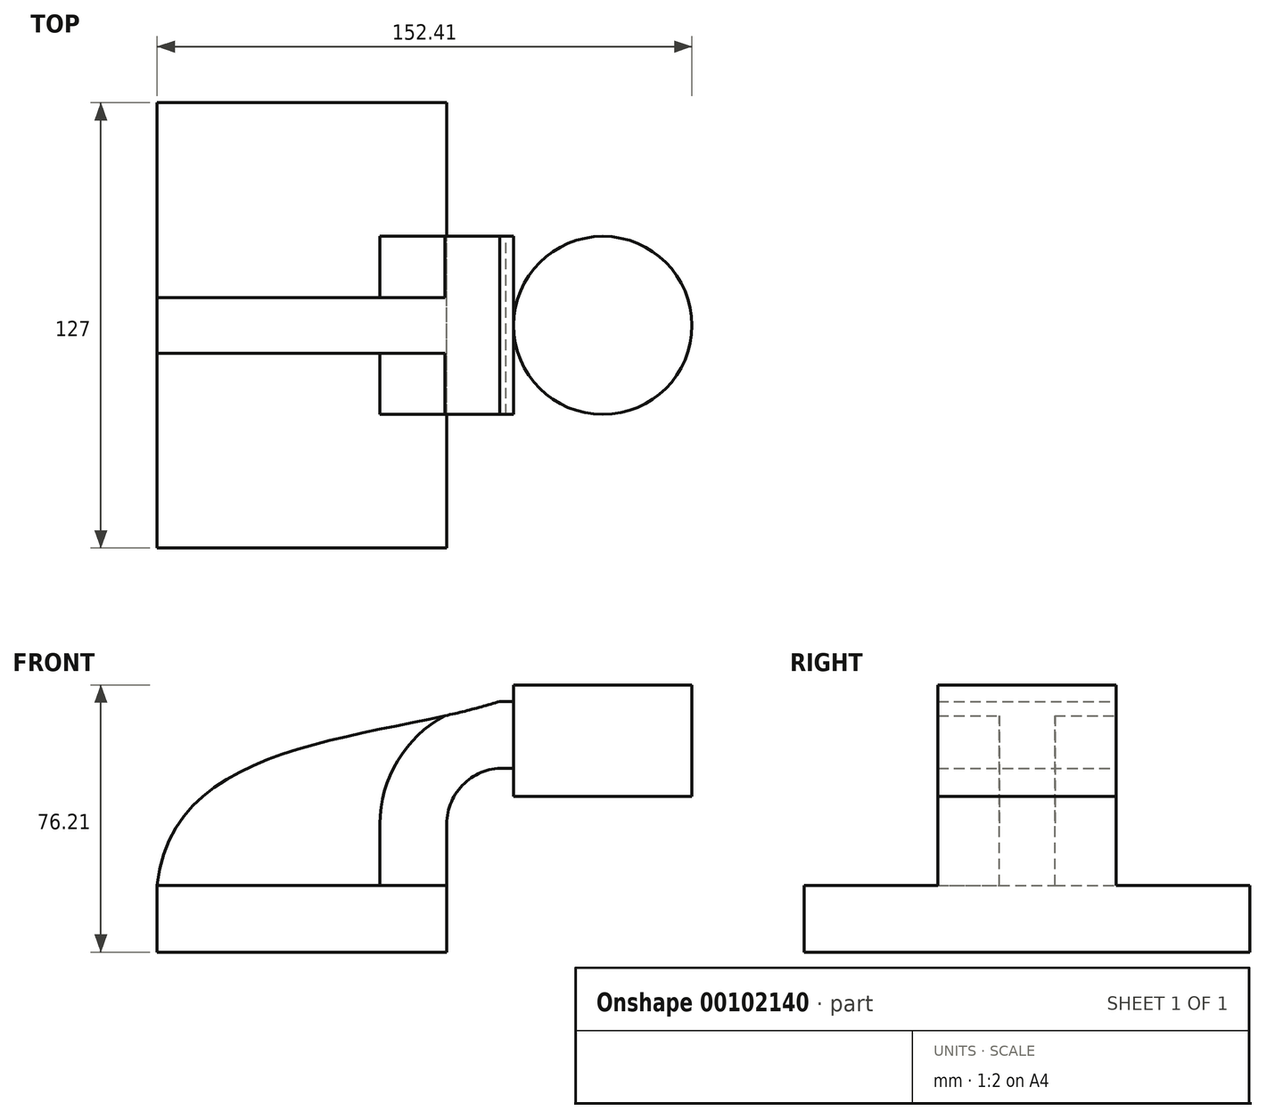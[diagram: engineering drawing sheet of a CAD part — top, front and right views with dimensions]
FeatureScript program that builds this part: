
annotation { "Feature Type Name" : "Feature", "Feature Type Description" : "" }
export const myFeature = defineFeature(function(context is Context, id is Id, definition is map)
    precondition{}
    {
        {
            var Q0;
            Q0=qCreatedBy(makeId("Front.planeOp"),FACE);
            var sketch = newSketch(context, id + "F0", { "sketchPlane" : qUnion([Q0])});
            skLineSegment(sketch, "E0.bottom", {"start": v(-41.28, 9.52) * mm, "end": v(41.28, 9.53) * mm});
            skLineSegment(sketch, "E0.top", {"start": v(-41.28, -9.53) * mm, "end": v(41.28, -9.53) * mm});
            skLineSegment(sketch, "E0.left", {"start": v(-41.28, 9.52) * mm, "end": v(-41.28, -9.53) * mm});
            skLineSegment(sketch, "E0.right", {"start": v(41.28, 9.53) * mm, "end": v(41.28, -9.52) * mm});
            skPoint(sketch, "E0.middle", {"position": v(0, 0) * mm});
            skLineSegment(sketch, "E1.bottom", {"start": v(60.32, 66.68) * mm, "end": v(111.12, 66.68) * mm});
            skLineSegment(sketch, "E1.top", {"start": v(60.32, 34.93) * mm, "end": v(111.12, 34.93) * mm});
            skLineSegment(sketch, "E1.left", {"start": v(60.32, 66.68) * mm, "end": v(60.32, 34.93) * mm});
            skLineSegment(sketch, "E1.right", {"start": v(111.12, 66.68) * mm, "end": v(111.12, 34.93) * mm});
            skPoint(sketch, "E1.middle", {"position": v(85.72, 50.8) * mm});
            skLineSegment(sketch, "E2", {"start": v(41.27, 9.53) * mm, "end": v(41.27, 27.03) * mm});
            skArc(sketch, "E3", {"start": v(41.27, 27.03) * mm, "mid": v(46.3, 38.61) * mm, "end": v(58.17, 42.88) * mm});
            skArc(sketch, "E4.1", {"start": v(22.22, 27.03) * mm, "mid": v(32.17, 51.44) * mm, "end": v(56.33, 61.95) * mm});
            skLineSegment(sketch, "E4.2", {"start": v(22.22, 9.53) * mm, "end": v(22.22, 27.03) * mm});
            skLineSegment(sketch, "E5", {"start": v(56.33, 61.95) * mm, "end": v(85.72, 61.95) * mm});
            skLineSegment(sketch, "E6", {"start": v(58.17, 42.88) * mm, "end": v(85.72, 42.88) * mm});
            skLineSegment(sketch, "E7", {"start": v(85.72, 34.93) * mm, "end": v(85.72, 66.68) * mm});
            skFitSpline(sketch, "E8", {"points": [v(-41.28, 9.52) * mm, v(56.33, 61.95) * mm], "startDerivative": vector(12.67, 127.2) * mm, "endDerivative": vector(106.31, 33.99) * mm});
            skSolve(sketch);
        }
        {
            var Q0;
            Q0=makeQuery(id+"F0.imprint","IMPRINT",FACE,{"disambiguationData":[TD([[makeQuery(id+"F0.imprint","IMPRINT",EDGE,{"derivedFrom":sQuery(id+"F0.wireOp",EDGE,"E0.top")}),1.0]])]});
            extrude(context, id + "F1", {"entities" : qUnion([Q0]), "endBound" : BoundingType.SYMMETRIC, "depth" : 127 * mm});
        }
        {
            var Q0;
            {var subQ7=sQuery(id+"F0.wireOp",EDGE,"E2");Q0=makeQuery(id+"F0.imprint","IMPRINT",FACE,{"disambiguationData":[TD([[makeQuery(id+"F0.imprint","IMPRINT",EDGE,{"derivedFrom":subQ7}),1.0]])]});}
            extrude(context, id + "F2", {"entities" : qUnion([Q0]), "operationType" : NewBodyOperationType.ADD, "endBound" : BoundingType.SYMMETRIC, "depth" : 50.8 * mm});
        }
        {
            var Q0;
            {var subQ3=sQuery(id+"F0.wireOp",EDGE,"E4.2");Q0=makeQuery(id+"F0.imprint","IMPRINT",FACE,{"disambiguationData":[TD([[makeQuery(id+"F0.imprint","IMPRINT",EDGE,{"derivedFrom":subQ3}),1.0]])]});}
            extrude(context, id + "F3", {"entities" : qUnion([Q0]), "operationType" : NewBodyOperationType.ADD, "endBound" : BoundingType.SYMMETRIC, "depth" : 15.88 * mm});
        }
        {
            var Q0;
            {var subQ0=sQuery(id+"F0.wireOp",EDGE,"E1.right");Q0=makeQuery(id+"F0.imprint","IMPRINT",FACE,{"disambiguationData":[TD([[makeQuery(id+"F0.imprint","IMPRINT",EDGE,{"derivedFrom":subQ0}),-1.0]])]});}
            var Q1;
            Q1=sQuery(id+"F0.wireOp",EDGE,"E7");
            revolve(context, id + "F4", {"operationType" : NewBodyOperationType.ADD, "entities" : qUnion([Q0]), "axis" : qUnion([Q1]), "revolveType" : RevolveType.FULL});
        }
    });
